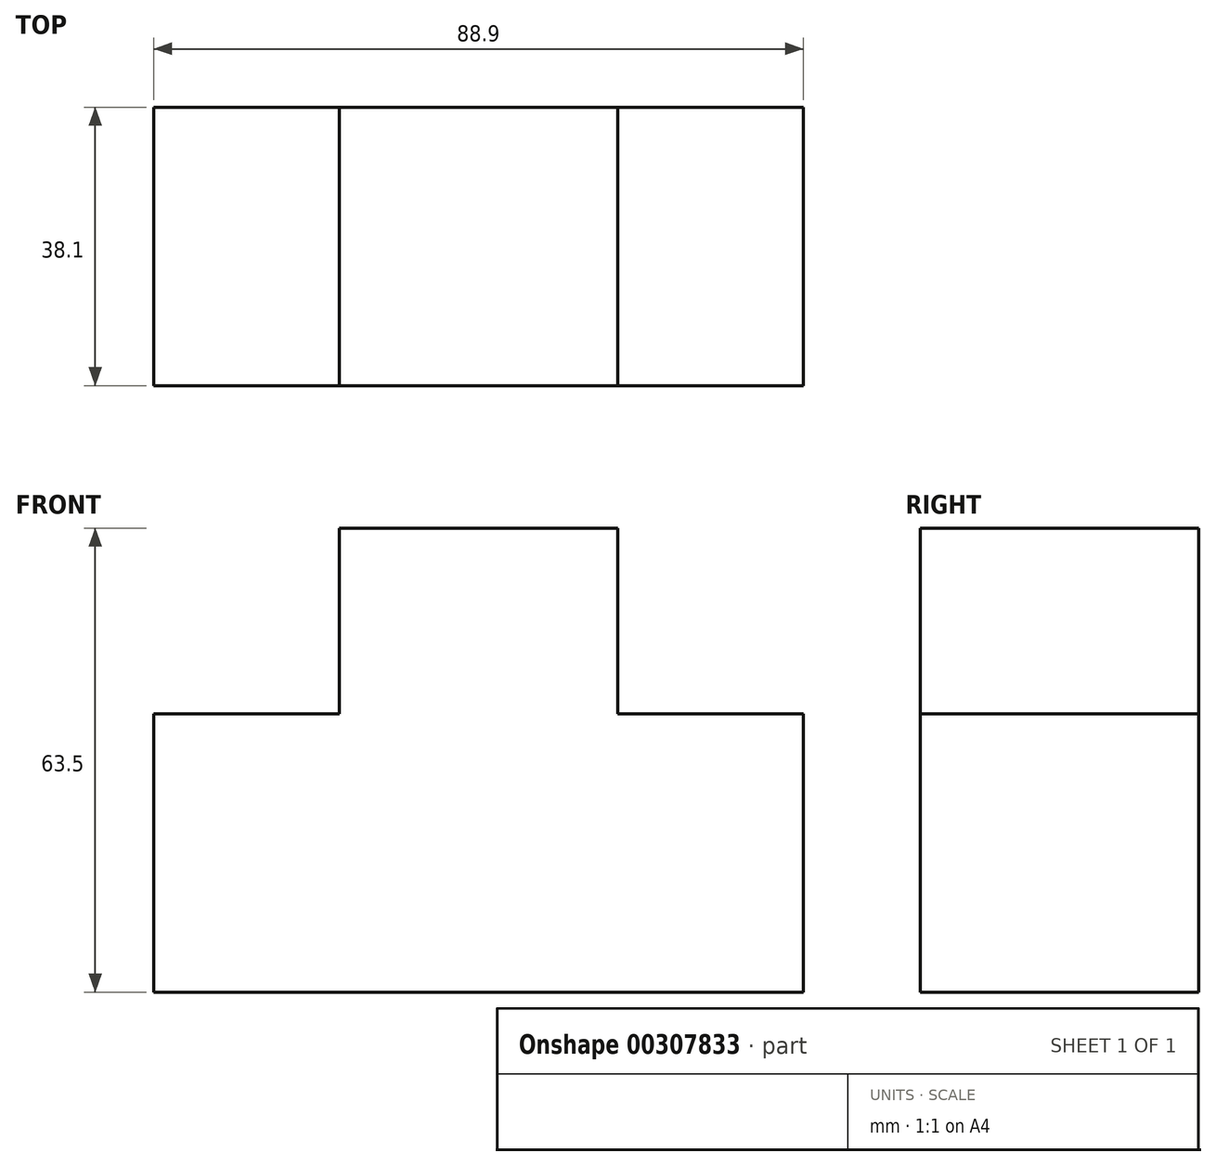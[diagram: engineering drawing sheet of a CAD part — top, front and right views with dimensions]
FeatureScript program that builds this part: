
annotation { "Feature Type Name" : "Feature", "Feature Type Description" : "" }
export const myFeature = defineFeature(function(context is Context, id is Id, definition is map)
    precondition{}
    {
        {
            var Q0;
            Q0=qCreatedBy(makeId("Front.planeOp"),FACE);
            var sketch = newSketch(context, id + "F0", { "sketchPlane" : qUnion([Q0])});
            skLineSegment(sketch, "E0", {"start": v(-16.25, 53.82) * mm, "end": v(21.85, 53.82) * mm});
            skLineSegment(sketch, "E1", {"start": v(21.85, 53.82) * mm, "end": v(21.85, 28.42) * mm});
            skLineSegment(sketch, "E2", {"start": v(-16.25, 53.82) * mm, "end": v(-16.25, 28.42) * mm});
            skLineSegment(sketch, "E3", {"start": v(-16.25, 28.42) * mm, "end": v(-41.65, 28.42) * mm});
            skLineSegment(sketch, "E4", {"start": v(21.85, 28.42) * mm, "end": v(47.25, 28.42) * mm});
            skLineSegment(sketch, "E5", {"start": v(-41.65, 28.42) * mm, "end": v(-41.65, -9.68) * mm});
            skLineSegment(sketch, "E6", {"start": v(-41.65, -9.68) * mm, "end": v(47.25, -9.68) * mm});
            skLineSegment(sketch, "E7", {"start": v(47.25, 28.42) * mm, "end": v(47.25, -9.68) * mm});
            skSolve(sketch);
        }
        {
            var Q0;
            Q0=makeQuery(id+"F0.imprint","IMPRINT",FACE,{"disambiguationData":[TD([[makeQuery(id+"F0.imprint","IMPRINT",EDGE,{"derivedFrom":sQuery(id+"F0.wireOp",EDGE,"E0")}),-1.0]])]});
            extrude(context, id + "F1", {"entities" : qUnion([Q0]), "depth" : 38.1 * mm});
        }
    });
